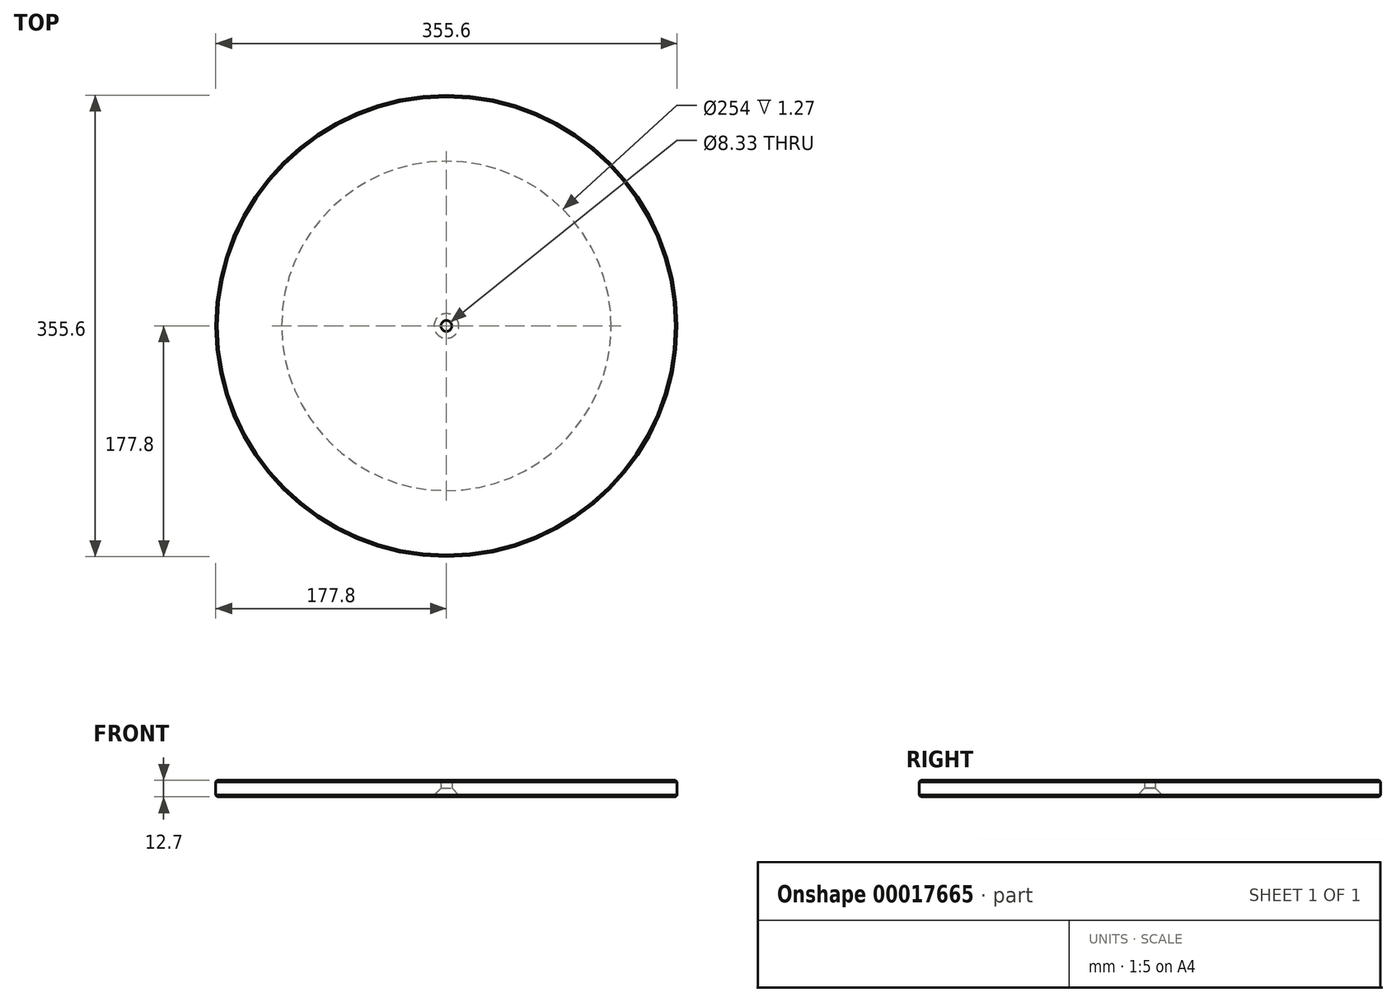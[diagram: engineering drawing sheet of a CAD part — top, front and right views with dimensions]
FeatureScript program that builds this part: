
annotation { "Feature Type Name" : "Feature", "Feature Type Description" : "" }
export const myFeature = defineFeature(function(context is Context, id is Id, definition is map)
    precondition{}
    {
        {
            var Q0;
            Q0=qCreatedBy(makeId("Top.planeOp"),FACE);
            var sketch = newSketch(context, id + "F0", { "sketchPlane" : qUnion([Q0])});
            skCircle(sketch, "E0", {"center": v(0, 0) * mm, "radius": 177.8 * mm});
            skSolve(sketch);
        }
        {
            var Q0;
            Q0 = qSketchRegion(id + "F0", true);
            extrude(context, id + "F1", {"entities" : qUnion([Q0]), "depth" : 12.7 * mm});
        }
        {
            var Q0;
            Q0=makeQuery(id+"F1.opExtrude","CAP_FACE",FACE,{"disambiguationData":[OSD([sQuery(id+"F0.wireOp",EDGE,"E0")])],"isStart":true});
            var sketch = newSketch(context, id + "F2", { "sketchPlane" : qUnion([Q0])});
            skCircle(sketch, "E1", {"center": v(0, 0) * mm, "radius": 127 * mm});
            skSolve(sketch);
        }
        {
            var Q0;
            Q0 = qSketchRegion(id + "F2", true);
            extrude(context, id + "F3", {"entities" : qUnion([Q0]), "operationType" : NewBodyOperationType.REMOVE, "oppositeDirection" : true, "depth" : 1.27 * mm});
        }
        {
            var Q0;
            Q0=makeQuery(id+"F3.boolean.opBoolean","COPY",FACE,{"derivedFrom":makeQuery(id+"F3.opExtrude","CAP_FACE",FACE,{"disambiguationData":[OSD([sQuery(id+"F2.wireOp",EDGE,"E1")])],"isStart":false})});
            var sketch = newSketch(context, id + "F4", { "sketchPlane" : qUnion([Q0])});
            skPoint(sketch, "E2", {"position": v(0, 0) * mm});
            skSolve(sketch);
        }
        {
            var Q0;
            Q0=sQuery(id+"F4.wireOp",VERTEX,"E2");
            var Q1;
            Q1=makeQuery(id+"F1.opExtrude","SWEPT_BODY",BODY,{"disambiguationData":[OSD([sQuery(id+"F0.wireOp",EDGE,"E0")])]});
            hole(context, id + "F5", {"style" : HoleStyle.C_SINK, "holeDiameter" : 8.33 * mm, "cSinkDiameter" : 19.05 * mm, "endStyle" : HoleEndStyle.THROUGH, "locations" : qUnion([Q0]), "scope" : qUnion([Q1]), "cSinkAngle" : 90 * degree});
        }
        {
            var Q0;
            Q0=makeQuery(id+"F1.opExtrude","SWEPT_FACE",FACE,{"disambiguationData":[OSD([sQuery(id+"F0.wireOp",EDGE,"E0")])]});
            chamfer(context, id + "F6", {"entities" : qUnion([Q0]), "width" : 1.27 * mm, "tangentPropagation" : true});
        }
    });
